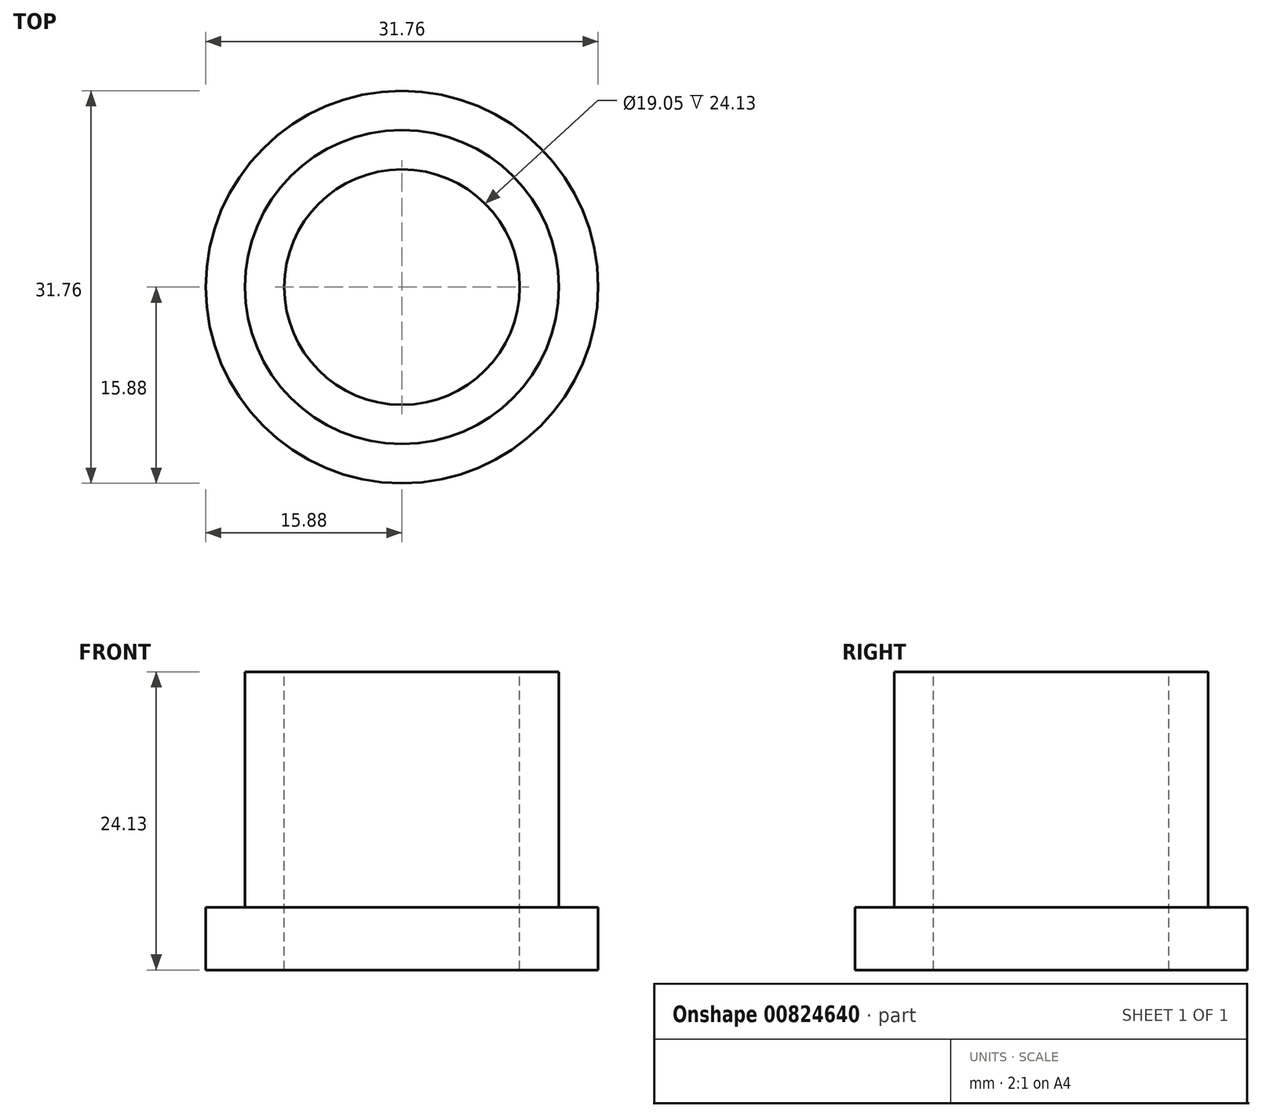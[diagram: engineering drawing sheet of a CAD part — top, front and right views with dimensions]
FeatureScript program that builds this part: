
annotation { "Feature Type Name" : "Feature", "Feature Type Description" : "" }
export const myFeature = defineFeature(function(context is Context, id is Id, definition is map)
    precondition{}
    {
        {
            var Q0;
            Q0=qCreatedBy(makeId("Top.planeOp"),FACE);
            var sketch = newSketch(context, id + "F0", { "sketchPlane" : qUnion([Q0])});
            skCircle(sketch, "E0", {"center": v(0, 0) * mm, "radius": 15.88 * mm});
            skSolve(sketch);
        }
        {
            var Q0;
            Q0 = qSketchRegion(id + "F0", true);
            extrude(context, id + "F1", {"entities" : qUnion([Q0]), "depth" : 5.08 * mm, "offsetDistance" : 25.4 * mm});
        }
        {
            var Q0;
            Q0=makeQuery(id+"F1.opExtrude","CAP_FACE",FACE,{"disambiguationData":[OSD([sQuery(id+"F0.wireOp",EDGE,"E0")])],"isStart":false});
            var sketch = newSketch(context, id + "F2", { "sketchPlane" : qUnion([Q0])});
            skCircle(sketch, "E1", {"center": v(0, 0) * mm, "radius": 12.7 * mm});
            skSolve(sketch);
        }
        {
            var Q0;
            Q0=makeQuery(id+"F2.imprint","IMPRINT",FACE,{"disambiguationData":[TD([[makeQuery(id+"F2.imprint","IMPRINT",EDGE,{"derivedFrom":sQuery(id+"F2.wireOp",EDGE,"E1")}),1.0]])]});
            extrude(context, id + "F3", {"entities" : qUnion([Q0]), "operationType" : NewBodyOperationType.ADD, "depth" : 19.05 * mm, "offsetDistance" : 25.4 * mm});
        }
        {
            var Q0;
            Q0=makeQuery(id+"F3.opExtrude","CAP_FACE",FACE,{"disambiguationData":[OSD([sQuery(id+"F2.wireOp",EDGE,"E1")])],"isStart":false});
            var sketch = newSketch(context, id + "F4", { "sketchPlane" : qUnion([Q0])});
            skCircle(sketch, "E2", {"center": v(0, 0) * mm, "radius": 9.53 * mm});
            skSolve(sketch);
        }
        {
            var Q0;
            Q0=makeQuery(id+"F4.imprint","IMPRINT",FACE,{"disambiguationData":[TD([[makeQuery(id+"F4.imprint","IMPRINT",EDGE,{"derivedFrom":sQuery(id+"F4.wireOp",EDGE,"E2")}),1.0]])]});
            extrude(context, id + "F5", {"entities" : qUnion([Q0]), "operationType" : NewBodyOperationType.REMOVE, "endBound" : BoundingType.THROUGH_ALL, "oppositeDirection" : true, "depth" : 25.4 * mm, "offsetDistance" : 25.4 * mm});
        }
    });
